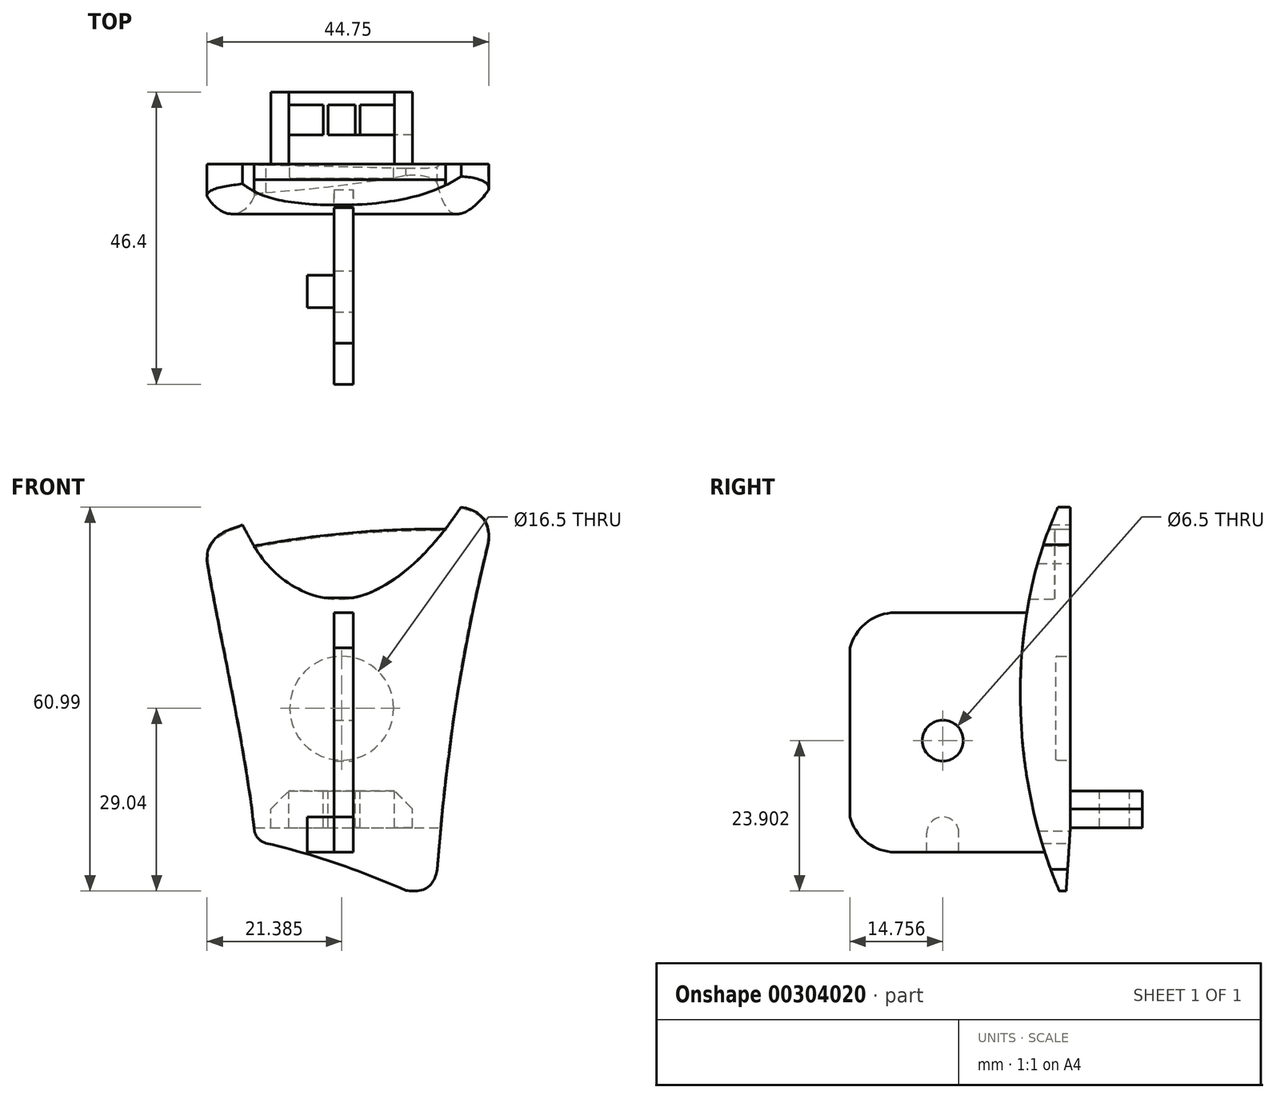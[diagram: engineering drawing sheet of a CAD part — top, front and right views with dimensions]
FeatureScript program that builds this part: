
annotation { "Feature Type Name" : "Feature", "Feature Type Description" : "" }
export const myFeature = defineFeature(function(context is Context, id is Id, definition is map)
    precondition{}
    {
        {
            var Q0;
            Q0=qCreatedBy(makeId("Front.planeOp"),FACE);
            var sketch = newSketch(context, id + "F0", { "sketchPlane" : qUnion([Q0])});
            skFitSpline(sketch, "E0", {"points": [v(149, -21.79) * mm, v(150.85, -19.85) * mm], "startDerivative": vector(2.52, 0.87) * mm, "endDerivative": vector(0.6, 3.2) * mm});
            skLineSegment(sketch, "E1", {"start": v(-11.58, -19.34) * mm, "end": v(10.92, -19.34) * mm});
            skLineSegment(sketch, "E2", {"start": v(-11.58, -19.34) * mm, "end": v(-11.58, -16.34) * mm});
            skLineSegment(sketch, "E3", {"start": v(-0.33, -19.34) * mm, "end": v(-0.33, -14.33) * mm, "construction": true});
            skLineSegment(sketch, "E4", {"start": v(-11.58, -16.34) * mm, "end": v(-8.74, -13.5) * mm});
            skLineSegment(sketch, "E5.MirrorCS", {"start": v(10.92, -16.34) * mm, "end": v(8.08, -13.5) * mm});
            skLineSegment(sketch, "E6.MirrorCS", {"start": v(10.92, -19.34) * mm, "end": v(10.92, -16.34) * mm});
            skLineSegment(sketch, "E7", {"start": v(-8.74, -13.5) * mm, "end": v(8.08, -13.5) * mm});
            skFitSpline(sketch, "E8.MirrorCS", {"points": [v(-12.34, -21.79) * mm, v(-14.19, -19.85) * mm], "startDerivative": vector(-2.52, 0.87) * mm, "endDerivative": vector(-0.6, 3.2) * mm});
            skLineSegment(sketch, "E9.MirrorCS", {"start": v(18.64, 31.6) * mm, "end": v(16.17, 28.12) * mm});
            skLineSegment(sketch, "E10.MirrorCS", {"start": v(-14.25, 25.43) * mm, "end": v(-16.08, 28.77) * mm});
            skFitSpline(sketch, "E11.MirrorCS", {"points": [v(-16.08, 28.77) * mm, v(-21.67, 22.65) * mm], "startDerivative": vector(-6.12, -2.2) * mm, "endDerivative": vector(1.47, -13.46) * mm});
            skFitSpline(sketch, "E12.MirrorCS", {"points": [v(9.87, -29.3) * mm, v(-12.34, -21.79) * mm], "startDerivative": vector(-20.99, 9.2) * mm, "endDerivative": vector(-22.91, 5.24) * mm});
            skFitSpline(sketch, "E13.MirrorCS", {"points": [v(14.86, -25.95) * mm, v(9.87, -29.3) * mm], "startDerivative": vector(-1.89, -9.59) * mm, "endDerivative": vector(-7.48, 1) * mm});
            skFitSpline(sketch, "E14.MirrorCS", {"points": [v(22.93, 25.61) * mm, v(18.64, 31.6) * mm], "startDerivative": vector(1.25, 7.98) * mm, "endDerivative": vector(-12.21, 1.98) * mm});
            skLineSegment(sketch, "E15.MirrorCS", {"start": v(0, 0) * mm, "end": v(0, 27.42) * mm});
            skFitSpline(sketch, "E16.MirrorCS", {"points": [v(22.93, 25.61) * mm, v(14.86, -25.95) * mm], "startDerivative": vector(-13, -51.37) * mm, "endDerivative": vector(-4.03, -52.05) * mm});
            skFitSpline(sketch, "E17.MirrorCS", {"points": [v(16.17, 28.12) * mm, v(-14.25, 25.43) * mm], "startDerivative": vector(-29, 0.24) * mm, "endDerivative": vector(-30.7, -5.75) * mm});
            skFitSpline(sketch, "E18.MirrorCS", {"points": [v(-21.67, 22.65) * mm, v(-14.19, -19.85) * mm], "startDerivative": vector(7.48, -42.5) * mm, "endDerivative": vector(4.94, -43.2) * mm});
            skSolve(sketch);
        }
        {
            var Q0;
            Q0=qCreatedBy(makeId("Right.planeOp"),FACE);
            var sketch = newSketch(context, id + "F1", { "sketchPlane" : qUnion([Q0])});
            skFitSpline(sketch, "E19", {"points": [v(0, -33.12) * mm, v(0, 35.58) * mm], "startDerivative": vector(-28.87, 56.38) * mm, "endDerivative": vector(34.58, 63.64) * mm});
            skLineSegment(sketch, "E20", {"start": v(0, 35.58) * mm, "end": v(0, 12.33) * mm});
            skLineSegment(sketch, "E21", {"start": v(-7.95, 1.96) * mm, "end": v(-7.95, -17.12) * mm});
            skSolve(sketch);
        }
        {
            var Q0;
            Q0=sQuery(id+"F1.wireOp",EDGE,"E19");
            extrude(context, id + "F2", {"bodyType" : ToolBodyType.SURFACE, "surfaceEntities" : qUnion([Q0]), "depth" : 25 * mm, "hasSecondDirection" : true, "secondDirectionOppositeDirection" : true, "secondDirectionDepth" : 25 * mm});
        }
        {
            var Q0;
            Q0=qSketchRegion(id+"F0",true);
            var Q1;
            Q1=makeQuery(id+"F0.imprint","IMPRINT",FACE,{"disambiguationData":[TD([[makeQuery(id+"F0.imprint","IMPRINT",EDGE,{"derivedFrom":sQuery(id+"F0.wireOp",EDGE,"E1")}),1.0]])]});
            extrude(context, id + "F3", {"entities" : qUnion([Q0, Q1]), "endBound" : BoundingType.UP_TO_NEXT, "depth" : 25 * mm});
        }
        {
            var Q0;
            Q0=qCreatedBy(makeId("Front.planeOp"),FACE);
            cPlane(context, id + "F4", {"entities" : qUnion([Q0]), "cplaneType" : CPlaneType.OFFSET, "offset" : 2.5 * mm, "width" : 150 * mm, "height" : 150 * mm});
        }
        {
            var Q0;
            Q0=qCreatedBy(id+"F4.planeOp",FACE);
            var sketch = newSketch(context, id + "F5", { "sketchPlane" : qUnion([Q0])});
            skFitSpline(sketch, "E22", {"points": [v(-14.23, 25.45) * mm, v(0, 17) * mm, v(16.16, 28.15) * mm], "startDerivative": vector(18.23, -32.66) * mm, "endDerivative": vector(24.32, 31.61) * mm});
            skFitSpline(sketch, "E23", {"points": [v(16.16, 28.15) * mm, v(-14.23, 25.45) * mm], "startDerivative": vector(-30.89, -0.18) * mm, "endDerivative": vector(-29.3, -6.33) * mm});
            skSolve(sketch);
        }
        {
            var Q0;
            Q0=qCreatedBy(makeId("Front.planeOp"),FACE);
            var sketch = newSketch(context, id + "F6", { "sketchPlane" : qUnion([Q0])});
            skLineSegment(sketch, "E24", {"start": v(1.5, 14.81) * mm, "end": v(1.5, -23.19) * mm});
            skLineSegment(sketch, "E25", {"start": v(0, -31.52) * mm, "end": v(0, 38.7) * mm, "construction": true});
            skLineSegment(sketch, "E26", {"start": v(1.5, 14.81) * mm, "end": v(0, 14.81) * mm});
            skLineSegment(sketch, "E27", {"start": v(1.5, -23.19) * mm, "end": v(0, -23.19) * mm});
            skLineSegment(sketch, "E28.MirrorCS", {"start": v(-1.5, 14.81) * mm, "end": v(0, 14.81) * mm});
            skLineSegment(sketch, "E29.MirrorCS", {"start": v(-1.5, 14.81) * mm, "end": v(-1.5, -23.19) * mm});
            skLineSegment(sketch, "E30.MirrorCS", {"start": v(-1.5, -23.19) * mm, "end": v(0, -23.19) * mm});
            skSolve(sketch);
        }
        {
            var Q0;
            Q0=qSketchRegion(id+"F6",true);
            extrude(context, id + "F7", {"entities" : qUnion([Q0]), "operationType" : NewBodyOperationType.ADD, "depth" : 35 * mm});
        }
        {
            var Q0;
            Q0=qSketchRegion(id+"F5",true);
            extrude(context, id + "F8", {"entities" : qUnion([Q0]), "operationType" : NewBodyOperationType.REMOVE, "depth" : 4 * mm});
        }
        {
            var Q0;
            Q0=makeQuery(id+"F0.imprint","IMPRINT",FACE,{"disambiguationData":[TD([[makeQuery(id+"F0.imprint","IMPRINT",EDGE,{"derivedFrom":sQuery(id+"F0.wireOp",EDGE,"E1")}),1.0]])]});
            extrude(context, id + "F9", {"entities" : qUnion([Q0]), "oppositeDirection" : true, "depth" : 4.6 * mm});
        }
        {
            var Q0;
            Q0=makeQuery(id+"F7.opExtrude","CAP_VERTEX",VERTEX,{"disambiguationData":[OSD([sQuery(id+"F6.wireOp",EDGE,"E24"),sQuery(id+"F6.wireOp",EDGE,"E26")])],"isStart":false});
            var Q1;
            Q1=makeQuery(id+"F7.opExtrude","CAP_VERTEX",VERTEX,{"disambiguationData":[OSD([sQuery(id+"F6.wireOp",EDGE,"E24"),sQuery(id+"F6.wireOp",EDGE,"E27")])],"isStart":false});
            var Q2;
            Q2=sQuery(id+"F6.wireOp",VERTEX,"E26.start");
            cPlane(context, id + "F10", {"entities" : qUnion([Q0, Q1, Q2]), "cplaneType" : CPlaneType.THREE_POINT, "offset" : 25 * mm, "width" : 150 * mm, "height" : 150 * mm});
        }
        {
            var Q0;
            Q0=qCreatedBy(id+"F10.planeOp",FACE);
            var sketch = newSketch(context, id + "F11", { "sketchPlane" : qUnion([Q0])});
            skLineSegment(sketch, "E31.MirrorCS", {"start": v(17.7, -23.19) * mm, "end": v(17.7, -20.19) * mm});
            skLineSegment(sketch, "E32.MirrorCS", {"start": v(17.7, -23.19) * mm, "end": v(20.24, -23.19) * mm});
            skLineSegment(sketch, "E33.MirrorCS", {"start": v(22.8, -23.19) * mm, "end": v(20.24, -23.19) * mm});
            skLineSegment(sketch, "E34.MirrorCS", {"start": v(22.8, -23.19) * mm, "end": v(22.8, -20.19) * mm});
            skLineSegment(sketch, "E35", {"start": v(20.24, -23.19) * mm, "end": v(20.24, -14.63) * mm, "construction": true});
            skArc(sketch, "E36", {"start": v(22.8, -20.19) * mm, "mid": v(20.24, -17.64) * mm, "end": v(17.7, -20.19) * mm});
            skSolve(sketch);
        }
        {
            var Q0;
            Q0=makeQuery(id+"F11.imprint","IMPRINT",FACE,{"disambiguationData":[TD([[makeQuery(id+"F11.imprint","IMPRINT",EDGE,{"derivedFrom":sQuery(id+"F11.wireOp",EDGE,"E31.MirrorCS")}),-1.0]])]});
            extrude(context, id + "F12", {"entities" : qUnion([Q0]), "operationType" : NewBodyOperationType.ADD, "depth" : 7.3 * mm});
        }
        {
            var Q0;
            Q0=qCreatedBy(id+"F10.planeOp",FACE);
            var sketch = newSketch(context, id + "F13", { "sketchPlane" : qUnion([Q0])});
            skArc(sketch, "E37", {"start": v(35, 9.25) * mm, "mid": v(32.6, 13.05) * mm, "end": v(28.44, 14.81) * mm});
            skLineSegment(sketch, "E38", {"start": v(28.44, 14.81) * mm, "end": v(35, 14.81) * mm});
            skLineSegment(sketch, "E39", {"start": v(35, 14.81) * mm, "end": v(35, 9.25) * mm});
            skLineSegment(sketch, "E40", {"start": v(35.11, -4.19) * mm, "end": v(13.07, -4.19) * mm, "construction": true});
            skArc(sketch, "E41.MirrorCS", {"start": v(35, -17.62) * mm, "mid": v(32.6, -21.43) * mm, "end": v(28.44, -23.19) * mm});
            skLineSegment(sketch, "E42.MirrorCS", {"start": v(35, -23.19) * mm, "end": v(35, -17.62) * mm});
            skLineSegment(sketch, "E43.MirrorCS", {"start": v(28.44, -23.19) * mm, "end": v(35, -23.19) * mm});
            skSolve(sketch);
        }
        {
            var Q0;
            Q0=qSketchRegion(id+"F13",true);
            extrude(context, id + "F14", {"entities" : qUnion([Q0]), "operationType" : NewBodyOperationType.REMOVE, "depth" : 25 * mm});
        }
        {
            var Q0;
            Q0=makeQuery(id+"F2.opExtrude","SWEPT_BODY",BODY,{"disambiguationData":[OSD([sQuery(id+"F1.wireOp",EDGE,"E19")])]});
            deleteBodies(context, id + "F15", {"entities" : qUnion([Q0])});
        }
        {
            var Q0;
            Q0=sQuery(id+"F0.wireOp",VERTEX,"E2.start");
            var Q1;
            Q1=sQuery(id+"F0.wireOp",VERTEX,"E4.start");
            var Q2;
            Q2=makeQuery(id+"F9.opExtrude","CAP_VERTEX",VERTEX,{"disambiguationData":[OSD([sQuery(id+"F0.wireOp",EDGE,"E1"),sQuery(id+"F0.wireOp",EDGE,"E2")])],"isStart":false});
            cPlane(context, id + "F16", {"entities" : qUnion([Q0, Q1, Q2]), "cplaneType" : CPlaneType.THREE_POINT, "offset" : 25 * mm, "width" : 150 * mm, "height" : 150 * mm});
        }
        {
            var Q0;
            Q0=qCreatedBy(id+"F16.planeOp",FACE);
            var sketch = newSketch(context, id + "F17", { "sketchPlane" : qUnion([Q0])});
            skLineSegment(sketch, "E44", {"start": v(0, -19.34) * mm, "end": v(0, -30.32) * mm, "construction": true});
            skLineSegment(sketch, "E45", {"start": v(0, -29.72) * mm, "end": v(-0.7, -29.72) * mm});
            skLineSegment(sketch, "E46", {"start": v(-0.7, -29.72) * mm, "end": v(0, -19.34) * mm});
            skLineSegment(sketch, "E47", {"start": v(0, -19.34) * mm, "end": v(0, -29.72) * mm});
            skSolve(sketch);
        }
        {
            var Q0;
            Q0=qSketchRegion(id+"F17",true);
            extrude(context, id + "F18", {"entities" : qUnion([Q0]), "operationType" : NewBodyOperationType.REMOVE, "endBound" : BoundingType.THROUGH_ALL, "oppositeDirection" : true, "depth" : 25 * mm, "hasSecondDirection" : true, "secondDirectionBound" : SecondDirectionBoundingType.THROUGH_ALL, "secondDirectionOppositeDirection" : false, "secondDirectionDepth" : 25 * mm});
        }
        {
            var Q0;
            Q0=qCreatedBy(makeId("Front.planeOp"),FACE);
            var sketch = newSketch(context, id + "F19", { "sketchPlane" : qUnion([Q0])});
            skLineSegment(sketch, "E48", {"start": v(-0.33, -13.5) * mm, "end": v(-0.33, -0.35) * mm, "construction": true});
            skCircle(sketch, "E49", {"center": v(-0.33, -0.35) * mm, "radius": 8.25 * mm});
            skSolve(sketch);
        }
        {
            var Q0;
            Q0=qSketchRegion(id+"F19",true);
            extrude(context, id + "F20", {"entities" : qUnion([Q0]), "operationType" : NewBodyOperationType.REMOVE, "depth" : 2.3 * mm});
        }
        {
            var Q0;
            {var subQ0=sQuery(id+"F19.wireOp",EDGE,"E49");Q0=makeQuery(id+"F20.boolean.opBoolean","COPY",EDGE,{"disambiguationData":[TD([makeQuery(id+"F20.opExtrude","SWEPT_FACE",FACE,{"disambiguationData":[OSD([subQ0])]}),makeQuery(id+"F20.opExtrude","CAP_FACE",FACE,{"disambiguationData":[OSD([subQ0])],"isStart":false})])],"derivedFrom":makeQuery(id+"F20.opExtrude","CAP_EDGE",EDGE,{"disambiguationData":[OSD([subQ0])],"isStart":false})});}
            var Q1;
            {var subQ0=sQuery(id+"F19.wireOp",EDGE,"E49");Q1=makeQuery(id+"F20.boolean.opBoolean","COPY",EDGE,{"disambiguationData":[topologyDisambiguationEdgeConnected([makeQuery(id+"F3.opExtrude","CAP_FACE",FACE,{"disambiguationData":[OSD([sQuery(id+"F0.wireOp",EDGE,"afdb6629-e3e9-4a31-9cc4-0ebf8e1a3909"),sQuery(id+"F0.wireOp",EDGE,"d147a2f3-9151-4835-866d-e3fd743a222a"),sQuery(id+"F0.wireOp",EDGE,"do7hIm2D-z98F-Ww93-GqAm-LJcrSVGsMmiP"),sQuery(id+"F0.wireOp",EDGE,"a36ab283-5ad5-483b-8515-050251eec640"),sQuery(id+"F0.wireOp",EDGE,"i9jpMKR7-9Wv5-1o8v-BlIj-OLvO2T6FqHY2"),sQuery(id+"F0.wireOp",EDGE,"d4f19420-3a88-4d4f-a6d5-182b0a20d642"),sQuery(id+"F0.wireOp",EDGE,"a69ab9b8-7286-4905-ad33-d6b5c325b92c"),sQuery(id+"F0.wireOp",EDGE,"552a9169-6fcc-4227-b7f1-2fae63d89aa0"),sQuery(id+"F0.wireOp",EDGE,"6c34fcdb-9c4d-49e7-8406-61af0e88d988"),sQuery(id+"F0.wireOp",EDGE,"E0")])],"isStart":true}),makeQuery(id+"F20.opExtrude","SWEPT_FACE",FACE,{"disambiguationData":[OSD([subQ0])]})])],"derivedFrom":makeQuery(id+"F20.opExtrude","CAP_EDGE",EDGE,{"disambiguationData":[OSD([subQ0])],"isStart":true})});}
            var Q2;
            Q2=makeQuery(id+"F3.opExtrude","CAP_EDGE",EDGE,{"disambiguationData":[OSD([sQuery(id+"F0.wireOp",EDGE,"a69ab9b8-7286-4905-ad33-d6b5c325b92c")])],"isStart":true});
            var Q3;
            Q3=makeQuery(id+"F3.opExtrude","CAP_EDGE",EDGE,{"disambiguationData":[OSD([sQuery(id+"F0.wireOp",EDGE,"afdb6629-e3e9-4a31-9cc4-0ebf8e1a3909")])],"isStart":true});
            var Q4;
            Q4=makeQuery(id+"F18.boolean.opBoolean","INTERSECT",EDGE,{"derivedFrom":[makeQuery(id+"F3.opExtrude","SWEPT_FACE",FACE,{"disambiguationData":[OSD([sQuery(id+"F0.wireOp",EDGE,"6c34fcdb-9c4d-49e7-8406-61af0e88d988")])]}),makeQuery(id+"F18.opExtrude","SWEPT_FACE",FACE,{"disambiguationData":[OSD([sQuery(id+"F17.wireOp",EDGE,"E46")])]})]});
            var Q5;
            Q5=makeQuery(id+"F18.boolean.opBoolean","INTERSECT",EDGE,{"derivedFrom":[makeQuery(id+"F3.opExtrude","SWEPT_FACE",FACE,{"disambiguationData":[OSD([sQuery(id+"F0.wireOp",EDGE,"552a9169-6fcc-4227-b7f1-2fae63d89aa0")])]}),makeQuery(id+"F18.opExtrude","SWEPT_FACE",FACE,{"disambiguationData":[OSD([sQuery(id+"F17.wireOp",EDGE,"E46")])]})]});
            var Q6;
            Q6=makeQuery(id+"F18.boolean.opBoolean","INTERSECT",EDGE,{"derivedFrom":[makeQuery(id+"F3.opExtrude","SWEPT_FACE",FACE,{"disambiguationData":[OSD([sQuery(id+"F0.wireOp",EDGE,"afdb6629-e3e9-4a31-9cc4-0ebf8e1a3909")])]}),makeQuery(id+"F18.opExtrude","SWEPT_FACE",FACE,{"disambiguationData":[OSD([sQuery(id+"F17.wireOp",EDGE,"E46")])]})]});
            var Q7;
            Q7=makeQuery(id+"F18.boolean.opBoolean","INTERSECT",EDGE,{"derivedFrom":[makeQuery(id+"F3.opExtrude","SWEPT_FACE",FACE,{"disambiguationData":[OSD([sQuery(id+"F0.wireOp",EDGE,"E0")])]}),makeQuery(id+"F18.opExtrude","SWEPT_FACE",FACE,{"disambiguationData":[OSD([sQuery(id+"F17.wireOp",EDGE,"E46")])]})]});
            var Q8;
            Q8=makeQuery(id+"F3.opExtrude","CAP_EDGE",EDGE,{"disambiguationData":[OSD([sQuery(id+"F0.wireOp",EDGE,"d147a2f3-9151-4835-866d-e3fd743a222a")])],"isStart":true});
            var Q9;
            Q9=makeQuery(id+"F3.opExtrude","CAP_EDGE",EDGE,{"disambiguationData":[OSD([sQuery(id+"F0.wireOp",EDGE,"d4f19420-3a88-4d4f-a6d5-182b0a20d642")])],"isStart":true});
            var Q10;
            Q10=makeQuery(id+"F3.opExtrude","CAP_EDGE",EDGE,{"disambiguationData":[OSD([sQuery(id+"F0.wireOp",EDGE,"E16.MirrorCS")])],"isStart":true});
            var Q11;
            Q11=makeQuery(id+"F3.opExtrude","CAP_EDGE",EDGE,{"disambiguationData":[OSD([sQuery(id+"F0.wireOp",EDGE,"E14.MirrorCS")])],"isStart":true});
            var Q12;
            Q12=makeQuery(id+"F3.opExtrude","CAP_EDGE",EDGE,{"disambiguationData":[OSD([sQuery(id+"F0.wireOp",EDGE,"E17.MirrorCS")])],"isStart":true});
            var Q13;
            Q13=makeQuery(id+"F3.opExtrude","CAP_EDGE",EDGE,{"disambiguationData":[OSD([sQuery(id+"F0.wireOp",EDGE,"E9.MirrorCS")])],"isStart":true});
            var Q14;
            Q14=makeQuery(id+"F3.opExtrude","CAP_EDGE",EDGE,{"disambiguationData":[OSD([sQuery(id+"F0.wireOp",EDGE,"E10.MirrorCS")])],"isStart":true});
            var Q15;
            Q15=makeQuery(id+"F3.opExtrude","CAP_EDGE",EDGE,{"disambiguationData":[OSD([sQuery(id+"F0.wireOp",EDGE,"E11.MirrorCS")])],"isStart":true});
            var Q16;
            Q16=makeQuery(id+"F3.opExtrude","CAP_EDGE",EDGE,{"disambiguationData":[OSD([sQuery(id+"F0.wireOp",EDGE,"E18.MirrorCS")])],"isStart":true});
            fillet(context, id + "F21", {"entities" : qUnion([Q0, Q1, Q2, Q3, Q4, Q5, Q6, Q7, Q8, Q9, Q10, Q11, Q12, Q13, Q14, Q15, Q16]), "radius" : 0.2 * mm, "tangentPropagation" : true, "allowEdgeOverflow" : false});
        }
        {
            var Q0;
            Q0=qCreatedBy(id+"F10.planeOp",FACE);
            var sketch = newSketch(context, id + "F22", { "sketchPlane" : qUnion([Q0])});
            skLineSegment(sketch, "E50", {"start": v(20.24, -23.19) * mm, "end": v(20.24, -5.49) * mm, "construction": true});
            skCircle(sketch, "E51", {"center": v(20.24, -5.49) * mm, "radius": 3.25 * mm});
            skSolve(sketch);
        }
        {
            var Q0;
            Q0 = qSketchRegion(id + "F22", true);
            extrude(context, id + "F23", {"entities" : qUnion([Q0]), "operationType" : NewBodyOperationType.REMOVE, "endBound" : BoundingType.THROUGH_ALL, "depth" : 25 * mm});
        }
        {
            var Q0;
            Q0=makeQuery(id+"F9.opExtrude","CAP_VERTEX",VERTEX,{"disambiguationData":[OSD([sQuery(id+"F0.wireOp",EDGE,"E1"),sQuery(id+"F0.wireOp",EDGE,"E6.MirrorCS")])],"isStart":false});
            var Q1;
            Q1=makeQuery(id+"F9.opExtrude","CAP_VERTEX",VERTEX,{"disambiguationData":[OSD([sQuery(id+"F0.wireOp",EDGE,"E5.MirrorCS"),sQuery(id+"F0.wireOp",EDGE,"E7")])],"isStart":false});
            var Q2;
            Q2=makeQuery(id+"F9.opExtrude","CAP_VERTEX",VERTEX,{"disambiguationData":[OSD([sQuery(id+"F0.wireOp",EDGE,"E1"),sQuery(id+"F0.wireOp",EDGE,"E2")])],"isStart":false});
            cPlane(context, id + "F24", {"entities" : qUnion([Q0, Q1, Q2]), "cplaneType" : CPlaneType.THREE_POINT, "offset" : 25 * mm, "width" : 150 * mm, "height" : 150 * mm});
        }
        {
            var Q0;
            Q0=qCreatedBy(id+"F24.planeOp",FACE);
            var sketch = newSketch(context, id + "F25", { "sketchPlane" : qUnion([Q0])});
            skLineSegment(sketch, "E52", {"start": v(11.58, -16.34) * mm, "end": v(11.58, -19.34) * mm});
            skLineSegment(sketch, "E53", {"start": v(11.58, -19.34) * mm, "end": v(8.74, -19.34) * mm});
            skLineSegment(sketch, "E54", {"start": v(8.74, -19.34) * mm, "end": v(8.74, -13.5) * mm});
            skLineSegment(sketch, "E55", {"start": v(8.74, -13.5) * mm, "end": v(11.58, -16.34) * mm});
            skLineSegment(sketch, "E56", {"start": v(8.74, -19.34) * mm, "end": v(3.23, -19.34) * mm, "construction": true});
            skLineSegment(sketch, "E57.bottom", {"start": v(3.23, -19.34) * mm, "end": v(2.48, -19.34) * mm});
            skLineSegment(sketch, "E57.top", {"start": v(3.23, -13.5) * mm, "end": v(2.48, -13.5) * mm});
            skLineSegment(sketch, "E57.left", {"start": v(3.23, -19.34) * mm, "end": v(3.23, -13.5) * mm});
            skLineSegment(sketch, "E57.right", {"start": v(2.48, -19.34) * mm, "end": v(2.48, -13.5) * mm});
            skLineSegment(sketch, "E58", {"start": v(0.33, -19.34) * mm, "end": v(0.33, -10.23) * mm, "construction": true});
            skLineSegment(sketch, "E59.MirrorCS", {"start": v(-2.57, -13.5) * mm, "end": v(-1.82, -13.5) * mm});
            skLineSegment(sketch, "E60.MirrorCS", {"start": v(-2.57, -19.34) * mm, "end": v(-1.82, -19.34) * mm});
            skLineSegment(sketch, "E61.MirrorCS", {"start": v(-2.57, -19.34) * mm, "end": v(-2.57, -13.5) * mm});
            skLineSegment(sketch, "E62.MirrorCS", {"start": v(-1.82, -19.34) * mm, "end": v(-1.82, -13.5) * mm});
            skLineSegment(sketch, "E63.MirrorCS", {"start": v(-10.92, -16.33) * mm, "end": v(-10.92, -19.33) * mm});
            skLineSegment(sketch, "E64.MirrorCS", {"start": v(-8.08, -19.33) * mm, "end": v(-8.08, -13.49) * mm});
            skLineSegment(sketch, "E65.MirrorCS", {"start": v(-8.08, -13.49) * mm, "end": v(-10.92, -16.33) * mm});
            skLineSegment(sketch, "E66.MirrorCS", {"start": v(-10.92, -19.33) * mm, "end": v(-8.08, -19.33) * mm});
            skSolve(sketch);
        }
        {
            var Q0;
            Q0 = qSketchRegion(id + "F25", true);
            extrude(context, id + "F26", {"entities" : qUnion([Q0]), "operationType" : NewBodyOperationType.ADD, "depth" : 4.8 * mm});
        }
        {
            var Q0;
            Q0=makeQuery(id+"F26.opExtrude","CAP_VERTEX",VERTEX,{"disambiguationData":[OSD([sQuery(id+"F25.wireOp",EDGE,"E53"),sQuery(id+"F25.wireOp",EDGE,"E54")])],"isStart":false});
            var Q1;
            Q1=makeQuery(id+"F26.opExtrude","CAP_VERTEX",VERTEX,{"disambiguationData":[OSD([sQuery(id+"F25.wireOp",EDGE,"E52"),sQuery(id+"F25.wireOp",EDGE,"E55")])],"isStart":false});
            var Q2;
            Q2=makeQuery(id+"F26.opExtrude","CAP_VERTEX",VERTEX,{"disambiguationData":[OSD([sQuery(id+"F25.wireOp",EDGE,"E63.MirrorCS"),sQuery(id+"F25.wireOp",EDGE,"E65.MirrorCS")])],"isStart":false});
            cPlane(context, id + "F27", {"entities" : qUnion([Q0, Q1, Q2]), "cplaneType" : CPlaneType.THREE_POINT, "offset" : 25 * mm, "width" : 150 * mm, "height" : 150 * mm});
        }
        {
            var Q0;
            Q0=qCreatedBy(id+"F27.planeOp",FACE);
            var sketch = newSketch(context, id + "F28", { "sketchPlane" : qUnion([Q0])});
            skLineSegment(sketch, "E67", {"start": v(-11.58, -16.34) * mm, "end": v(-11.58, -19.34) * mm});
            skLineSegment(sketch, "E68", {"start": v(-11.58, -19.34) * mm, "end": v(10.92, -19.33) * mm});
            skLineSegment(sketch, "E69", {"start": v(10.92, -19.33) * mm, "end": v(10.92, -16.33) * mm});
            skLineSegment(sketch, "E70", {"start": v(10.92, -16.33) * mm, "end": v(8.08, -13.49) * mm});
            skLineSegment(sketch, "E71", {"start": v(-8.74, -13.5) * mm, "end": v(-11.58, -16.34) * mm});
            skLineSegment(sketch, "E72", {"start": v(-8.74, -13.5) * mm, "end": v(8.08, -13.49) * mm});
            skSolve(sketch);
        }
        {
            var Q0;
            Q0 = qSketchRegion(id + "F28", true);
            extrude(context, id + "F29", {"entities" : qUnion([Q0]), "operationType" : NewBodyOperationType.ADD, "oppositeDirection" : true, "depth" : 2 * mm});
        }
    });
